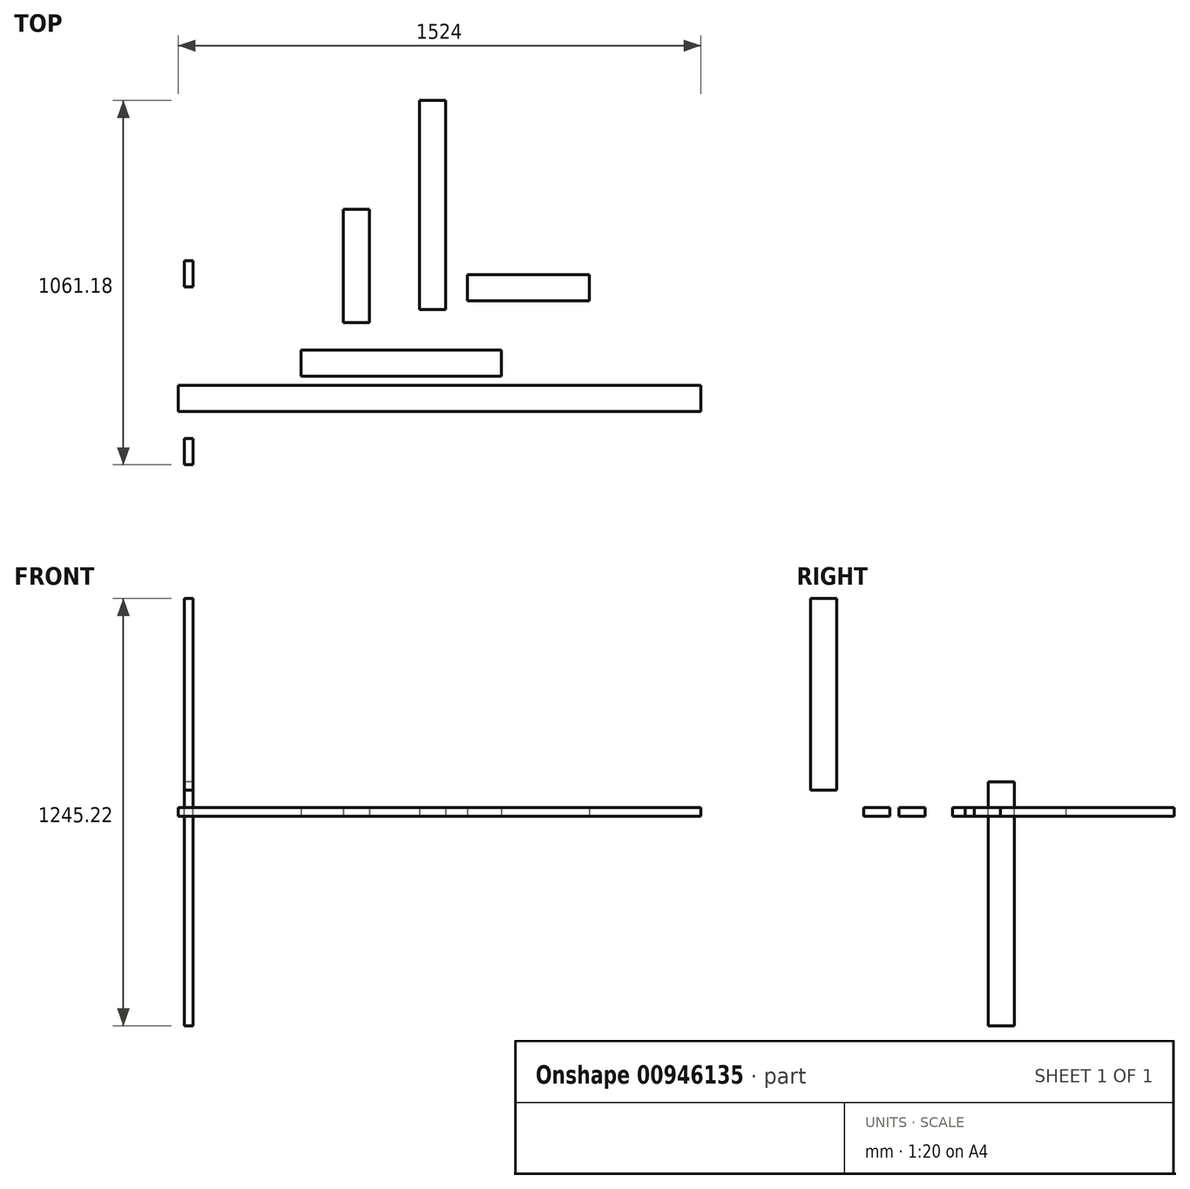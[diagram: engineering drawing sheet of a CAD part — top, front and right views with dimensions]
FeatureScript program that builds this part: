
annotation { "Feature Type Name" : "Feature", "Feature Type Description" : "" }
export const myFeature = defineFeature(function(context is Context, id is Id, definition is map)
    precondition{}
    {
        {
            var Q0;
            Q0=qCreatedBy(makeId("Top.planeOp"),FACE);
            var sketch = newSketch(context, id + "F0", { "sketchPlane" : qUnion([Q0])});
            skLineSegment(sketch, "E0.bottom", {"start": v(-17.61, 28.96) * mm, "end": v(1506.39, 28.96) * mm});
            skLineSegment(sketch, "E0.top", {"start": v(-17.61, 105.16) * mm, "end": v(1506.39, 105.16) * mm});
            skLineSegment(sketch, "E0.left", {"start": v(-17.61, 28.96) * mm, "end": v(-17.61, 105.16) * mm});
            skLineSegment(sketch, "E0.right", {"start": v(1506.39, 28.96) * mm, "end": v(1506.39, 105.16) * mm});
            skSolve(sketch);
        }
        {
            var Q0;
            Q0 = qSketchRegion(id + "F0", true);
            extrude(context, id + "F1", {"entities" : qUnion([Q0]), "depth" : 25.4 * mm, "offsetDistance" : 25.4 * mm});
        }
        {
            var Q0;
            Q0=qCreatedBy(makeId("Right.planeOp"),FACE);
            var sketch = newSketch(context, id + "F2", { "sketchPlane" : qUnion([Q0])});
            skLineSegment(sketch, "E1.bottom", {"start": v(468.63, -610.71) * mm, "end": v(392.43, -610.71) * mm});
            skLineSegment(sketch, "E1.top", {"start": v(468.63, 100.49) * mm, "end": v(392.43, 100.49) * mm});
            skLineSegment(sketch, "E1.left", {"start": v(468.63, -610.71) * mm, "end": v(468.63, 100.49) * mm});
            skLineSegment(sketch, "E1.right", {"start": v(392.43, -610.71) * mm, "end": v(392.43, 100.49) * mm});
            skSolve(sketch);
        }
        {
            var Q0;
            Q0=makeQuery(id+"F2.imprint","IMPRINT",FACE,{"disambiguationData":[TD([[makeQuery(id+"F2.imprint","IMPRINT",EDGE,{"derivedFrom":sQuery(id+"F2.wireOp",EDGE,"E1.bottom")}),-1.0]])]});
            extrude(context, id + "F3", {"entities" : qUnion([Q0]), "depth" : 25.4 * mm, "offsetDistance" : 25.4 * mm});
        }
        {
            var Q0;
            Q0=qCreatedBy(makeId("Right.planeOp"),FACE);
            var sketch = newSketch(context, id + "F4", { "sketchPlane" : qUnion([Q0])});
            skLineSegment(sketch, "E2.bottom", {"start": v(-49.97, 75.7) * mm, "end": v(-126.17, 75.7) * mm});
            skLineSegment(sketch, "E2.top", {"start": v(-49.97, 634.5) * mm, "end": v(-126.17, 634.5) * mm});
            skLineSegment(sketch, "E2.left", {"start": v(-49.97, 75.7) * mm, "end": v(-49.97, 634.5) * mm});
            skLineSegment(sketch, "E2.right", {"start": v(-126.17, 75.7) * mm, "end": v(-126.17, 634.5) * mm});
            skSolve(sketch);
        }
        {
            var Q0;
            Q0 = qSketchRegion(id + "F4", true);
            extrude(context, id + "F5", {"entities" : qUnion([Q0]), "depth" : 25.4 * mm, "offsetDistance" : 25.4 * mm});
        }
        {
            var Q0;
            Q0=qCreatedBy(makeId("Top.planeOp"),FACE);
            var sketch = newSketch(context, id + "F6", { "sketchPlane" : qUnion([Q0])});
            skLineSegment(sketch, "E3.bottom", {"start": v(464.23, 288.3) * mm, "end": v(540.43, 288.3) * mm});
            skLineSegment(sketch, "E3.top", {"start": v(464.23, 618.5) * mm, "end": v(540.43, 618.5) * mm});
            skLineSegment(sketch, "E3.left", {"start": v(464.23, 288.3) * mm, "end": v(464.23, 618.5) * mm});
            skLineSegment(sketch, "E3.right", {"start": v(540.43, 288.3) * mm, "end": v(540.43, 618.5) * mm});
            skSolve(sketch);
        }
        {
            var Q0;
            Q0 = qSketchRegion(id + "F6", true);
            extrude(context, id + "F7", {"entities" : qUnion([Q0]), "depth" : 25.4 * mm, "offsetDistance" : 25.4 * mm});
        }
        {
            var Q0;
            Q0=qCreatedBy(makeId("Top.planeOp"),FACE);
            var sketch = newSketch(context, id + "F8", { "sketchPlane" : qUnion([Q0])});
            skLineSegment(sketch, "E4.bottom", {"start": v(340.98, 131.6) * mm, "end": v(925.18, 131.6) * mm});
            skLineSegment(sketch, "E4.top", {"start": v(340.98, 207.8) * mm, "end": v(925.18, 207.8) * mm});
            skLineSegment(sketch, "E4.left", {"start": v(340.98, 131.6) * mm, "end": v(340.98, 207.8) * mm});
            skLineSegment(sketch, "E4.right", {"start": v(925.18, 131.6) * mm, "end": v(925.18, 207.8) * mm});
            skSolve(sketch);
        }
        {
            var Q0;
            Q0 = qSketchRegion(id + "F8", true);
            extrude(context, id + "F9", {"entities" : qUnion([Q0]), "depth" : 25.4 * mm, "offsetDistance" : 25.4 * mm});
        }
        {
            var Q0;
            Q0=qCreatedBy(makeId("Top.planeOp"),FACE);
            var sketch = newSketch(context, id + "F10", { "sketchPlane" : qUnion([Q0])});
            skLineSegment(sketch, "E5.bottom", {"start": v(762.12, 325.41) * mm, "end": v(685.92, 325.41) * mm});
            skLineSegment(sketch, "E5.top", {"start": v(762.12, 935.01) * mm, "end": v(685.92, 935.01) * mm});
            skLineSegment(sketch, "E5.left", {"start": v(762.12, 325.41) * mm, "end": v(762.12, 935.01) * mm});
            skLineSegment(sketch, "E5.right", {"start": v(685.92, 325.41) * mm, "end": v(685.92, 935.01) * mm});
            skSolve(sketch);
        }
        {
            var Q0;
            Q0=makeQuery(id+"F10.imprint","IMPRINT",FACE,{"disambiguationData":[TD([[makeQuery(id+"F10.imprint","IMPRINT",EDGE,{"derivedFrom":sQuery(id+"F10.wireOp",EDGE,"E5.bottom")}),-1.0]])]});
            extrude(context, id + "F11", {"entities" : qUnion([Q0]), "depth" : 25.4 * mm, "offsetDistance" : 25.4 * mm});
        }
        {
            var Q0;
            Q0=qCreatedBy(makeId("Top.planeOp"),FACE);
            var sketch = newSketch(context, id + "F12", { "sketchPlane" : qUnion([Q0])});
            skLineSegment(sketch, "E6.bottom", {"start": v(825.45, 427.24) * mm, "end": v(1181.05, 427.24) * mm});
            skLineSegment(sketch, "E6.top", {"start": v(825.45, 351.04) * mm, "end": v(1181.05, 351.04) * mm});
            skLineSegment(sketch, "E6.left", {"start": v(825.45, 427.24) * mm, "end": v(825.45, 351.04) * mm});
            skLineSegment(sketch, "E6.right", {"start": v(1181.05, 427.24) * mm, "end": v(1181.05, 351.04) * mm});
            skSolve(sketch);
        }
        {
            var Q0;
            Q0=makeQuery(id+"F12.imprint","IMPRINT",FACE,{"disambiguationData":[TD([[makeQuery(id+"F12.imprint","IMPRINT",EDGE,{"derivedFrom":sQuery(id+"F12.wireOp",EDGE,"E6.bottom")}),-1.0]])]});
            extrude(context, id + "F13", {"entities" : qUnion([Q0]), "depth" : 25.4 * mm, "offsetDistance" : 25.4 * mm});
        }
    });
